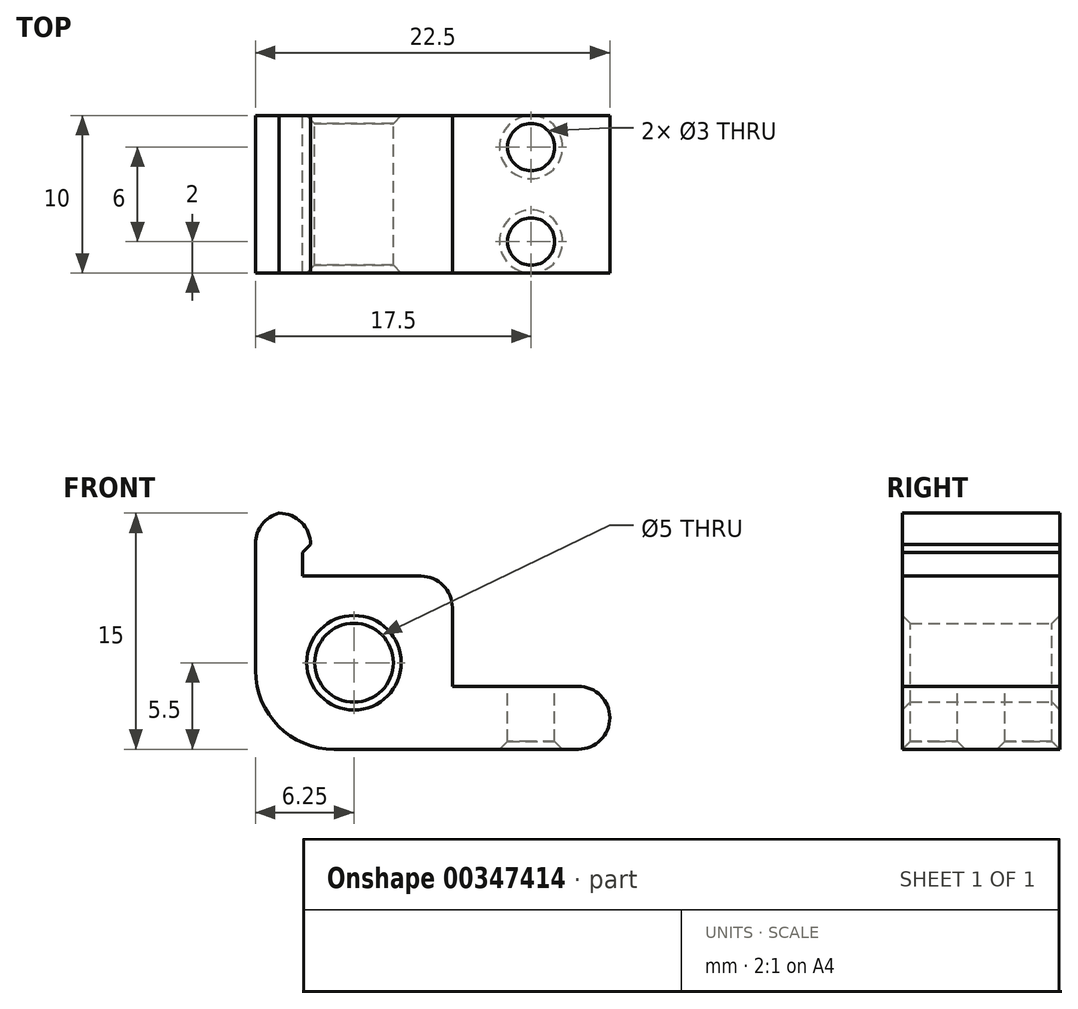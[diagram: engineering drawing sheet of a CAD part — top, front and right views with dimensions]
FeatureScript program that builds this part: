
annotation { "Feature Type Name" : "Feature", "Feature Type Description" : "" }
export const myFeature = defineFeature(function(context is Context, id is Id, definition is map)
    precondition{}
    {
        {
            var Q0;
            Q0=qCreatedBy(makeId("Front.planeOp"),FACE);
            var sketch = newSketch(context, id + "F0", { "sketchPlane" : qUnion([Q0])});
            skLineSegment(sketch, "E0.bottom", {"start": v(-6.25, 9.5) * mm, "end": v(-2.75, 9.5) * mm});
            skLineSegment(sketch, "E0.top", {"start": v(-6.25, -5.5) * mm, "end": v(16.25, -5.5) * mm});
            skLineSegment(sketch, "E0.left", {"start": v(-6.25, 9.5) * mm, "end": v(-6.25, -5.5) * mm});
            skLineSegment(sketch, "E0.right", {"start": v(16.25, -1.5) * mm, "end": v(16.25, -5.5) * mm});
            skLineSegment(sketch, "E1", {"start": v(-2.75, 9.5) * mm, "end": v(-2.75, 7.5) * mm});
            skLineSegment(sketch, "E2", {"start": v(-2.75, 7.5) * mm, "end": v(-3.25, 7) * mm});
            skLineSegment(sketch, "E3", {"start": v(-3.25, 7) * mm, "end": v(-3.25, 5.5) * mm});
            skLineSegment(sketch, "E4", {"start": v(-3.25, 5.5) * mm, "end": v(6.25, 5.5) * mm});
            skLineSegment(sketch, "E5", {"start": v(6.25, 5.5) * mm, "end": v(6.25, -1.5) * mm});
            skLineSegment(sketch, "E6", {"start": v(6.25, -1.5) * mm, "end": v(16.25, -1.5) * mm});
            skLineSegment(sketch, "E7", {"start": v(6.25, 5.5) * mm, "end": v(-6.25, -5.5) * mm, "construction": true});
            skCircle(sketch, "E8", {"center": v(0, 0) * mm, "radius": 2.5 * mm});
            skSolve(sketch);
        }
        {
            var Q0;
            Q0 = qSketchRegion(id + "F0", true);
            extrude(context, id + "F1", {"entities" : qUnion([Q0]), "depth" : 10 * mm});
        }
        {
            var Q0;
            Q0=makeQuery(id+"F1.opExtrude","SWEPT_FACE",FACE,{"disambiguationData":[OSD([sQuery(id+"F0.wireOp",EDGE,"E6")])]});
            var sketch = newSketch(context, id + "F2", { "sketchPlane" : qUnion([Q0])});
            skCircle(sketch, "E9", {"center": v(11.25, -8) * mm, "radius": 1.5 * mm});
            skCircle(sketch, "E10", {"center": v(11.25, -2) * mm, "radius": 1.5 * mm});
            skSolve(sketch);
        }
        {
            var Q0;
            Q0 = qSketchRegion(id + "F2", true);
            extrude(context, id + "F3", {"entities" : qUnion([Q0]), "operationType" : NewBodyOperationType.REMOVE, "oppositeDirection" : true, "depth" : 25 * mm});
        }
        {
            var Q0;
            Q0=makeQuery(id+"F1.opExtrude","SWEPT_EDGE",EDGE,{"disambiguationData":[OSD([sQuery(id+"F0.wireOp",EDGE,"E0.bottom"),sQuery(id+"F0.wireOp",EDGE,"E1")])]});
            fillet(context, id + "F4", {"entities" : qUnion([Q0]), "radius" : 2 * mm, "tangentPropagation" : true, "allowEdgeOverflow" : false});
        }
        {
            var Q0;
            Q0=makeQuery(id+"F1.opExtrude","SWEPT_EDGE",EDGE,{"disambiguationData":[OSD([sQuery(id+"F0.wireOp",EDGE,"E0.bottom"),sQuery(id+"F0.wireOp",EDGE,"E0.left")])]});
            fillet(context, id + "F5", {"entities" : qUnion([Q0]), "radius" : 2 * mm, "tangentPropagation" : true, "allowEdgeOverflow" : false});
        }
        {
            var Q0;
            Q0=makeQuery(id+"F1.opExtrude","SWEPT_EDGE",EDGE,{"disambiguationData":[OSD([sQuery(id+"F0.wireOp",EDGE,"E0.top"),sQuery(id+"F0.wireOp",EDGE,"E0.left")])]});
            fillet(context, id + "F6", {"entities" : qUnion([Q0]), "radius" : 5 * mm, "tangentPropagation" : true, "allowEdgeOverflow" : false});
        }
        {
            var Q0;
            Q0=makeQuery(id+"F1.opExtrude","SWEPT_EDGE",EDGE,{"disambiguationData":[OSD([sQuery(id+"F0.wireOp",EDGE,"E4"),sQuery(id+"F0.wireOp",EDGE,"E5")])]});
            fillet(context, id + "F7", {"entities" : qUnion([Q0]), "radius" : 2 * mm, "tangentPropagation" : true, "allowEdgeOverflow" : false});
        }
        {
            var Q0;
            Q0=makeQuery(id+"F1.opExtrude","SWEPT_EDGE",EDGE,{"disambiguationData":[OSD([sQuery(id+"F0.wireOp",EDGE,"E0.right"),sQuery(id+"F0.wireOp",EDGE,"E6")])]});
            var Q1;
            Q1=makeQuery(id+"F1.opExtrude","SWEPT_EDGE",EDGE,{"disambiguationData":[OSD([sQuery(id+"F0.wireOp",EDGE,"E0.top"),sQuery(id+"F0.wireOp",EDGE,"E0.right")])]});
            fillet(context, id + "F8", {"entities" : qUnion([Q0, Q1]), "radius" : 2 * mm, "tangentPropagation" : true, "allowEdgeOverflow" : false});
        }
        {
            var Q0;
            Q0=makeQuery(id+"F3.boolean.opBoolean","INTERSECT",EDGE,{"derivedFrom":[makeQuery(id+"F1.opExtrude","SWEPT_FACE",FACE,{"disambiguationData":[OSD([sQuery(id+"F0.wireOp",EDGE,"E0.top")])]}),makeQuery(id+"F3.opExtrude","SWEPT_FACE",FACE,{"disambiguationData":[OSD([sQuery(id+"F2.wireOp",EDGE,"E9")])]})]});
            var Q1;
            Q1=makeQuery(id+"F3.boolean.opBoolean","INTERSECT",EDGE,{"derivedFrom":[makeQuery(id+"F1.opExtrude","SWEPT_FACE",FACE,{"disambiguationData":[OSD([sQuery(id+"F0.wireOp",EDGE,"E0.top")])]}),makeQuery(id+"F3.opExtrude","SWEPT_FACE",FACE,{"disambiguationData":[OSD([sQuery(id+"F2.wireOp",EDGE,"E10")])]})]});
            chamfer(context, id + "F9", {"entities" : qUnion([Q0, Q1]), "width" : 0.5 * mm, "tangentPropagation" : true});
        }
        {
            var Q0;
            Q0=makeQuery(id+"F1.opExtrude","CAP_EDGE",EDGE,{"disambiguationData":[OSD([sQuery(id+"F0.wireOp",EDGE,"E8")])],"isStart":false});
            var Q1;
            Q1=makeQuery(id+"F1.opExtrude","CAP_EDGE",EDGE,{"disambiguationData":[OSD([sQuery(id+"F0.wireOp",EDGE,"E8")])],"isStart":true});
            chamfer(context, id + "F10", {"entities" : qUnion([Q0, Q1]), "width" : 0.5 * mm, "tangentPropagation" : true});
        }
    });
